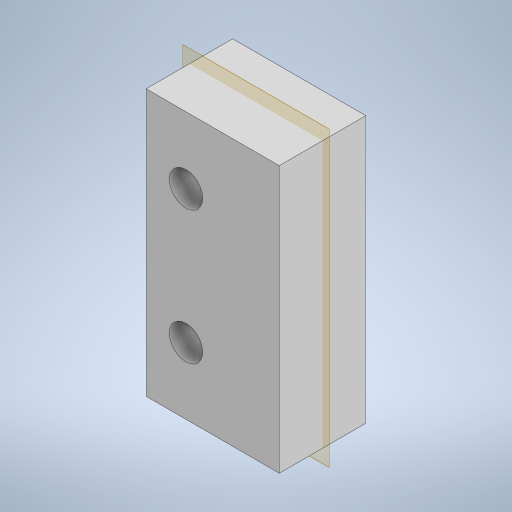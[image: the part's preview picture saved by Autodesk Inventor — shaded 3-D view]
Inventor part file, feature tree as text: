
AUTODESK INVENTOR PART (.ipt)
format: ipt  version: 2024 (Build 280153000, 153)  size: 223,744 bytes
history: native  units: mm
features: extrude x2, sketch x2, plane x1, projected_geometry x1
ambient origin geometry x8: Origin, YZ Plane, XZ Plane, XY Plane, X Axis, Y Axis, Z Axis, Center Point
bodies: Solid1 (feature_tree)
feature tree (6):
  extrude  "Extrusion1"  Depth=20.0mm
  extrude  "Extrusion2"  Depth=6.5mm
  plane  "Work Plane1"
  sketch  "Sketch1"  dims[d0=10.0mm d1=20.0mm]
  sketch  "Sketch2"  dims[d2=6.5mm d3=0.0mm d4=5.0mm d5=2.5mm d6=3.0mm d7=5.0mm d8=3.0mm d9=2.5mm d10=0.0mm d11=0.0mm]
  projected_geometry  "Projected Loop1"
